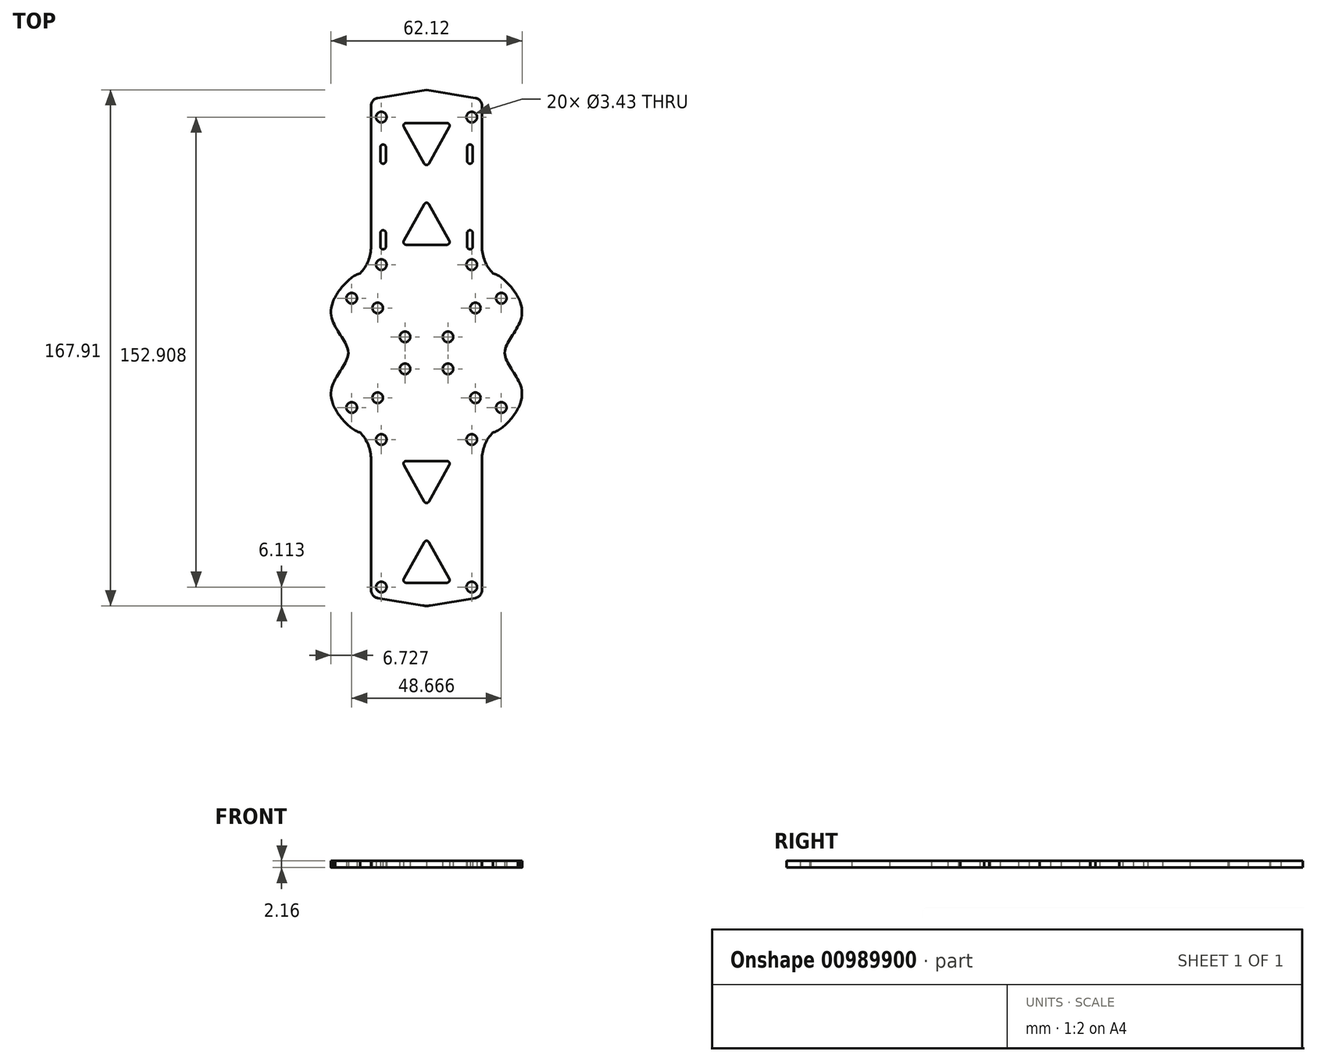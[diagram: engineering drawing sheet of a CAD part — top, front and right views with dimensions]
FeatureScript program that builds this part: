
annotation { "Feature Type Name" : "Feature", "Feature Type Description" : "" }
export const myFeature = defineFeature(function(context is Context, id is Id, definition is map)
    precondition{}
    {
        {
            var Q0;
            Q0=qCreatedBy(makeId("Top.planeOp"),FACE);
            var sketch = newSketch(context, id + "F0", { "sketchPlane" : qUnion([Q0])});
            skLineSegment(sketch, "E0", {"start": v(0, 116.91) * mm, "end": v(0, -116.2) * mm, "construction": true});
            skLineSegment(sketch, "E1", {"start": v(-18.03, -36.26) * mm, "end": v(-18.03, -78.82) * mm});
            skLineSegment(sketch, "E2", {"start": v(-15.92, 81.32) * mm, "end": v(0, 84.01) * mm});
            skPoint(sketch, "E3.visualSharp", {"position": v(-18.03, 80.96) * mm});
            skArc(sketch, "E3.filletArc", {"start": v(-15.92, 81.32) * mm, "mid": v(-17.43, 80.46) * mm, "end": v(-18.03, 78.82) * mm});
            skLineSegment(sketch, "E4", {"start": v(-15.92, -81.32) * mm, "end": v(-1.27, -83.8) * mm});
            skPoint(sketch, "E5.visualSharp", {"position": v(-18.03, -80.96) * mm});
            skArc(sketch, "E5.filletArc", {"start": v(-18.03, -78.82) * mm, "mid": v(-17.43, -80.46) * mm, "end": v(-15.92, -81.32) * mm});
            skFitSpline(sketch, "E6", {"points": [v(-18.03, 30.04) * mm, v(-30.48, 14.93) * mm, v(-25.4, -1.59) * mm, v(-30.48, -18.1) * mm, v(-18.03, -22.52) * mm], "startDerivative": vector(0, -61.8) * mm, "endDerivative": vector(0, 144.45) * mm});
            skLineSegment(sketch, "E7", {"start": v(-18.03, 78.82) * mm, "end": v(-18.03, 33.09) * mm});
            skArc(sketch, "E8.filletArc", {"start": v(-22.47, 23.45) * mm, "mid": v(-19.2, 27.78) * mm, "end": v(-18.03, 33.09) * mm});
            skCircle(sketch, "E9", {"center": v(-6.99, 3.62) * mm, "radius": 1.71 * mm});
            skCircle(sketch, "E10", {"center": v(-15.89, 13.03) * mm, "radius": 1.71 * mm});
            skCircle(sketch, "E11", {"center": v(-24.33, 16.2) * mm, "radius": 1.71 * mm});
            skLineSegment(sketch, "E12", {"start": v(-25.4, -1.59) * mm, "end": v(0, -1.59) * mm, "construction": true});
            skCircle(sketch, "E13.MirrorC", {"center": v(-6.99, -6.8) * mm, "radius": 1.71 * mm});
            skCircle(sketch, "E14.MirrorC", {"center": v(-15.89, -16.2) * mm, "radius": 1.71 * mm});
            skCircle(sketch, "E15.MirrorC", {"center": v(-24.33, -19.37) * mm, "radius": 1.71 * mm});
            skCircle(sketch, "E16", {"center": v(-14.7, 75.12) * mm, "radius": 1.71 * mm});
            skCircle(sketch, "E17", {"center": v(-14.7, 27.11) * mm, "radius": 1.71 * mm});
            skCircle(sketch, "E18", {"center": v(-14.7, -77.79) * mm, "radius": 1.71 * mm});
            skCircle(sketch, "E19", {"center": v(-14.7, -29.78) * mm, "radius": 1.71 * mm});
            skLineSegment(sketch, "E20", {"start": v(0, 73.22) * mm, "end": v(-6.6, 73.22) * mm});
            skLineSegment(sketch, "E21", {"start": v(-7.38, 71.88) * mm, "end": v(-0.79, 60.02) * mm});
            skLineSegment(sketch, "E22", {"start": v(-0.79, 46.78) * mm, "end": v(-7.38, 34.93) * mm});
            skLineSegment(sketch, "E23", {"start": v(-6.6, 33.6) * mm, "end": v(0, 33.6) * mm});
            skPoint(sketch, "E24.visualSharp", {"position": v(-8.13, 73.22) * mm});
            skArc(sketch, "E24.filletArc", {"start": v(-6.6, 73.22) * mm, "mid": v(-7.37, 72.77) * mm, "end": v(-7.38, 71.88) * mm});
            skPoint(sketch, "E25.visualSharp", {"position": v(-8.13, 33.6) * mm});
            skArc(sketch, "E25.filletArc", {"start": v(-7.38, 34.93) * mm, "mid": v(-7.37, 34.04) * mm, "end": v(-6.6, 33.6) * mm});
            skArc(sketch, "E26.MirrorCS", {"start": v(6.6, 73.22) * mm, "mid": v(7.37, 72.77) * mm, "end": v(7.38, 71.88) * mm});
            skArc(sketch, "E27.MirrorCS", {"start": v(15.92, 81.32) * mm, "mid": v(17.43, 80.46) * mm, "end": v(18.03, 78.82) * mm});
            skArc(sketch, "E28.MirrorCS", {"start": v(7.38, 34.93) * mm, "mid": v(7.37, 34.04) * mm, "end": v(6.6, 33.6) * mm});
            skCircle(sketch, "E29.MirrorC", {"center": v(14.7, -77.79) * mm, "radius": 1.71 * mm});
            skArc(sketch, "E30.MirrorCS", {"start": v(22.47, 23.45) * mm, "mid": v(19.2, 27.78) * mm, "end": v(18.03, 33.09) * mm});
            skArc(sketch, "E31.MirrorCS", {"start": v(18.03, -78.82) * mm, "mid": v(17.43, -80.46) * mm, "end": v(15.92, -81.32) * mm});
            skCircle(sketch, "E32.MirrorC", {"center": v(14.7, 27.11) * mm, "radius": 1.71 * mm});
            skCircle(sketch, "E33.MirrorC", {"center": v(14.7, -29.78) * mm, "radius": 1.71 * mm});
            skCircle(sketch, "E34.MirrorC", {"center": v(14.7, 75.12) * mm, "radius": 1.71 * mm});
            skLineSegment(sketch, "E35.MirrorCS", {"start": v(0, 73.22) * mm, "end": v(6.6, 73.22) * mm});
            skCircle(sketch, "E36.MirrorC", {"center": v(24.33, -19.37) * mm, "radius": 1.71 * mm});
            skLineSegment(sketch, "E37.MirrorCS", {"start": v(7.38, 71.88) * mm, "end": v(0.79, 60.02) * mm});
            skCircle(sketch, "E38.MirrorC", {"center": v(6.99, -6.8) * mm, "radius": 1.71 * mm});
            skLineSegment(sketch, "E39.MirrorCS", {"start": v(6.6, 33.6) * mm, "end": v(0, 33.6) * mm});
            skCircle(sketch, "E40.MirrorC", {"center": v(15.89, -16.2) * mm, "radius": 1.71 * mm});
            skCircle(sketch, "E41.MirrorC", {"center": v(6.99, 3.62) * mm, "radius": 1.71 * mm});
            skCircle(sketch, "E42.MirrorC", {"center": v(15.89, 13.03) * mm, "radius": 1.71 * mm});
            skCircle(sketch, "E43.MirrorC", {"center": v(24.33, 16.2) * mm, "radius": 1.71 * mm});
            skPoint(sketch, "E44.MirrorP", {"position": v(8.13, 73.22) * mm});
            skLineSegment(sketch, "E45.MirrorCS", {"start": v(15.92, -81.32) * mm, "end": v(1.27, -83.8) * mm});
            skPoint(sketch, "E46.MirrorP", {"position": v(18.03, -27.65) * mm});
            skPoint(sketch, "E47.MirrorP", {"position": v(18.03, 80.96) * mm});
            skLineSegment(sketch, "E48.MirrorCS", {"start": v(25.4, -1.59) * mm, "end": v(0, -1.59) * mm, "construction": true});
            skPoint(sketch, "E49.MirrorP", {"position": v(18.03, 30.04) * mm});
            skPoint(sketch, "E50.MirrorP", {"position": v(18.03, -80.96) * mm});
            skLineSegment(sketch, "E51.MirrorCS", {"start": v(18.03, -36.26) * mm, "end": v(18.03, -78.82) * mm});
            skFitSpline(sketch, "E52.MirrorCS", {"points": [v(18.03, 30.04) * mm, v(30.48, 14.93) * mm, v(25.4, -1.59) * mm, v(30.48, -18.1) * mm, v(18.03, -22.52) * mm], "startDerivative": vector(0, -61.8) * mm, "endDerivative": vector(0, 144.45) * mm});
            skLineSegment(sketch, "E53.MirrorCS", {"start": v(18.03, 78.82) * mm, "end": v(18.03, 33.09) * mm});
            skLineSegment(sketch, "E54.MirrorCS", {"start": v(0.79, 46.78) * mm, "end": v(7.38, 34.93) * mm});
            skLineSegment(sketch, "E55.MirrorCS", {"start": v(15.92, 81.32) * mm, "end": v(0, 84.01) * mm});
            skPoint(sketch, "E56.MirrorP", {"position": v(8.13, 33.6) * mm});
            skPoint(sketch, "E57.visualSharp", {"position": v(0, 48.2) * mm});
            skArc(sketch, "E57.filletArc", {"start": v(0.79, 46.78) * mm, "mid": v(0, 47.24) * mm, "end": v(-0.79, 46.78) * mm});
            skPoint(sketch, "E58.visualSharp", {"position": v(0, 58.61) * mm});
            skArc(sketch, "E58.filletArc", {"start": v(-0.79, 60.02) * mm, "mid": v(0, 59.56) * mm, "end": v(0.79, 60.02) * mm});
            skPoint(sketch, "E59.visualSharp", {"position": v(0, -84.01) * mm});
            skArc(sketch, "E59.filletArc", {"start": v(-1.27, -83.8) * mm, "mid": v(0, -83.9) * mm, "end": v(1.27, -83.8) * mm});
            skArc(sketch, "E60.MirrorCS", {"start": v(7.38, -38.1) * mm, "mid": v(7.37, -37.21) * mm, "end": v(6.6, -36.77) * mm});
            skLineSegment(sketch, "E61.MirrorCS", {"start": v(6.6, -36.77) * mm, "end": v(0, -36.77) * mm});
            skLineSegment(sketch, "E62.MirrorCS", {"start": v(-6.6, -36.77) * mm, "end": v(0, -36.77) * mm});
            skArc(sketch, "E63.MirrorCS", {"start": v(-7.38, -38.1) * mm, "mid": v(-7.37, -37.21) * mm, "end": v(-6.6, -36.77) * mm});
            skLineSegment(sketch, "E64.MirrorCS", {"start": v(-0.79, -49.96) * mm, "end": v(-7.38, -38.1) * mm});
            skArc(sketch, "E65.MirrorCS", {"start": v(0.79, -49.96) * mm, "mid": v(0, -50.42) * mm, "end": v(-0.79, -49.96) * mm});
            skArc(sketch, "E66.MirrorCS", {"start": v(-0.79, -63.2) * mm, "mid": v(0, -62.74) * mm, "end": v(0.79, -63.2) * mm});
            skLineSegment(sketch, "E67.MirrorCS", {"start": v(7.38, -75.05) * mm, "end": v(0.79, -63.2) * mm});
            skArc(sketch, "E68.MirrorCS", {"start": v(6.6, -76.4) * mm, "mid": v(7.37, -75.95) * mm, "end": v(7.38, -75.05) * mm});
            skLineSegment(sketch, "E69.MirrorCS", {"start": v(0, -76.4) * mm, "end": v(6.6, -76.4) * mm});
            skLineSegment(sketch, "E70.MirrorCS", {"start": v(0, -76.4) * mm, "end": v(-6.6, -76.4) * mm});
            skLineSegment(sketch, "E71.MirrorCS", {"start": v(-7.38, -75.05) * mm, "end": v(-0.79, -63.2) * mm});
            skArc(sketch, "E72.MirrorCS", {"start": v(-6.6, -76.4) * mm, "mid": v(-7.37, -75.95) * mm, "end": v(-7.38, -75.05) * mm});
            skLineSegment(sketch, "E73.MirrorCS", {"start": v(0.79, -49.96) * mm, "end": v(7.38, -38.1) * mm});
            skArc(sketch, "E74", {"start": v(-13.23, 65.32) * mm, "mid": v(-14.12, 66.2) * mm, "end": v(-15.01, 65.32) * mm});
            skArc(sketch, "E75", {"start": v(-15.01, 60.87) * mm, "mid": v(-14.12, 59.98) * mm, "end": v(-13.23, 60.87) * mm});
            skArc(sketch, "E76", {"start": v(-13.23, 37.43) * mm, "mid": v(-14.12, 38.32) * mm, "end": v(-15.01, 37.43) * mm});
            skArc(sketch, "E77", {"start": v(-15.01, 32.98) * mm, "mid": v(-14.12, 32.1) * mm, "end": v(-13.23, 32.98) * mm});
            skLineSegment(sketch, "E78", {"start": v(-15.01, 65.32) * mm, "end": v(-15.01, 60.87) * mm});
            skLineSegment(sketch, "E79", {"start": v(-13.23, 65.32) * mm, "end": v(-13.23, 60.87) * mm});
            skLineSegment(sketch, "E80", {"start": v(-15.01, 37.43) * mm, "end": v(-15.01, 32.98) * mm});
            skLineSegment(sketch, "E81", {"start": v(-13.23, 37.43) * mm, "end": v(-13.23, 32.98) * mm});
            skArc(sketch, "E82.MirrorCS", {"start": v(13.23, 65.32) * mm, "mid": v(14.12, 66.2) * mm, "end": v(15.01, 65.32) * mm});
            skLineSegment(sketch, "E83.MirrorCS", {"start": v(15.01, 65.32) * mm, "end": v(15.01, 60.87) * mm});
            skLineSegment(sketch, "E84.MirrorCS", {"start": v(13.23, 65.32) * mm, "end": v(13.23, 60.87) * mm});
            skArc(sketch, "E85.MirrorCS", {"start": v(15.01, 60.87) * mm, "mid": v(14.12, 59.98) * mm, "end": v(13.23, 60.87) * mm});
            skArc(sketch, "E86.MirrorCS", {"start": v(13.23, 37.43) * mm, "mid": v(14.12, 38.32) * mm, "end": v(15.01, 37.43) * mm});
            skLineSegment(sketch, "E87.MirrorCS", {"start": v(13.23, 37.43) * mm, "end": v(13.23, 32.98) * mm});
            skLineSegment(sketch, "E88.MirrorCS", {"start": v(15.01, 37.43) * mm, "end": v(15.01, 32.98) * mm});
            skArc(sketch, "E89.MirrorCS", {"start": v(15.01, 32.98) * mm, "mid": v(14.12, 32.1) * mm, "end": v(13.23, 32.98) * mm});
            skPoint(sketch, "E90.MirrorCS.end.orphan", {"position": v(23.8, -26.44) * mm});
            skFitSpline(sketch, "E91.MirrorCS", {"points": [v(-18.03, -33.21) * mm, v(-30.48, -18.1) * mm, v(-25.4, -1.59) * mm, v(-30.48, 14.92) * mm, v(-18.03, 19.35) * mm], "startDerivative": vector(0, 61.8) * mm, "endDerivative": vector(0, -144.45) * mm});
            skArc(sketch, "E92.MirrorCS", {"start": v(-22.47, -26.62) * mm, "mid": v(-19.2, -30.96) * mm, "end": v(-18.03, -36.26) * mm});
            skFitSpline(sketch, "E93.MirrorCS", {"points": [v(18.03, -33.21) * mm, v(30.48, -18.1) * mm, v(25.4, -1.59) * mm, v(30.48, 14.92) * mm, v(18.03, 19.35) * mm], "startDerivative": vector(0, 61.8) * mm, "endDerivative": vector(0, -144.45) * mm});
            skArc(sketch, "E94.MirrorCS", {"start": v(22.47, -26.62) * mm, "mid": v(19.2, -30.96) * mm, "end": v(18.03, -36.26) * mm});
            skSolve(sketch);
        }
        {
            var Q0;
            Q0 = qSketchRegion(id + "F0", true);
            extrude(context, id + "F1", {"entities" : qUnion([Q0]), "depth" : 2.16 * mm, "offsetDistance" : 25.4 * mm});
        }
    });
